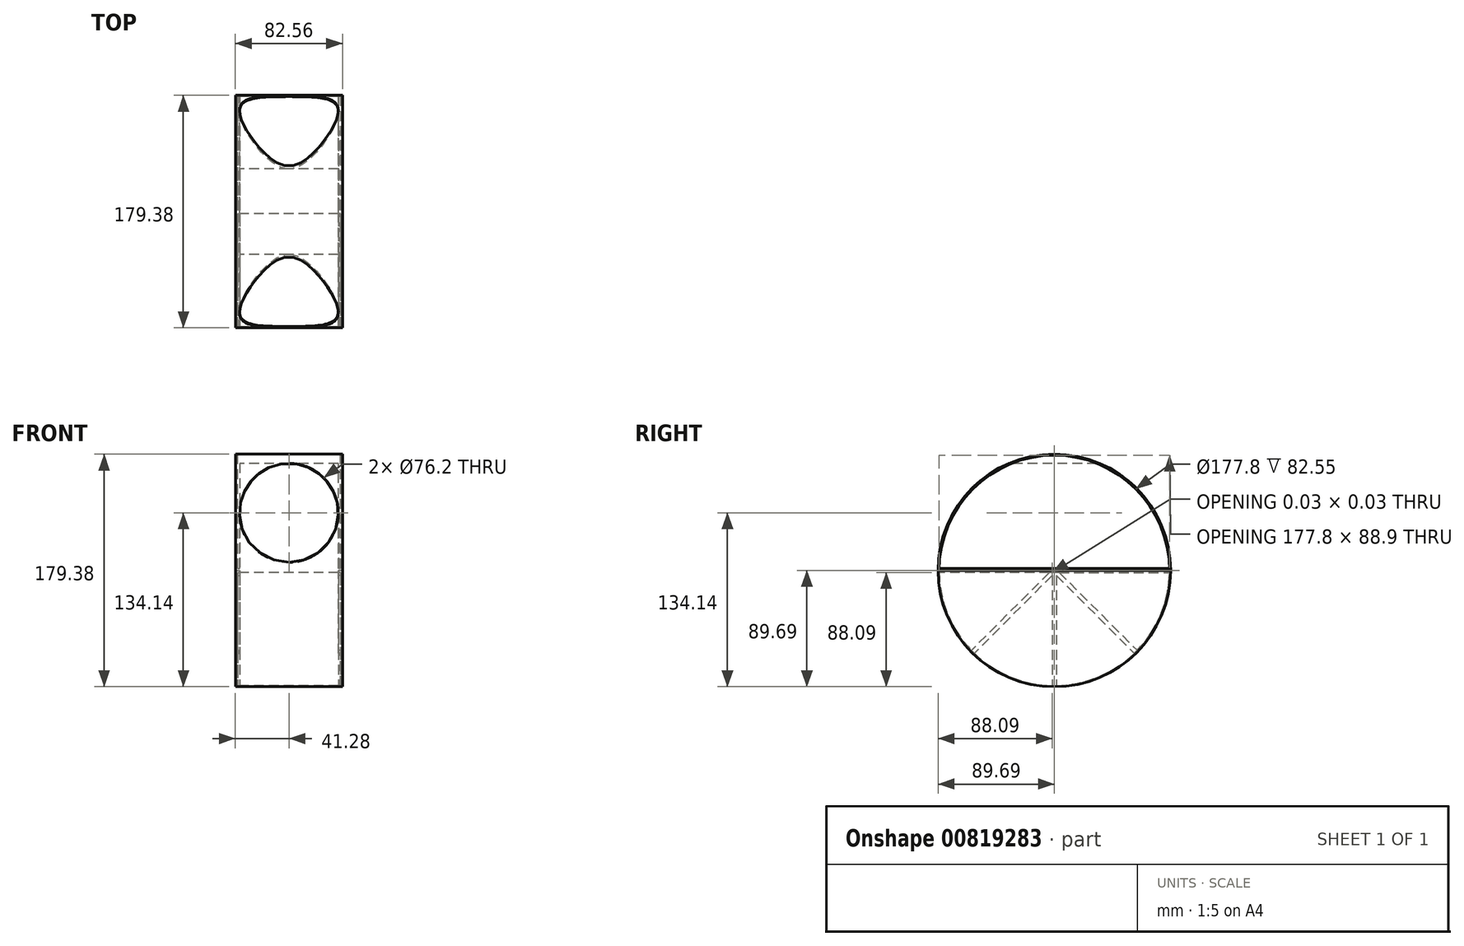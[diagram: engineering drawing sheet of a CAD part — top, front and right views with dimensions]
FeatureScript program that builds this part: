
annotation { "Feature Type Name" : "Feature", "Feature Type Description" : "" }
export const myFeature = defineFeature(function(context is Context, id is Id, definition is map)
    precondition{}
    {
        {
            var Q0;
            Q0=qCreatedBy(makeId("Right.planeOp"),FACE);
            var sketch = newSketch(context, id + "F0", { "sketchPlane" : qUnion([Q0])});
            skCircle(sketch, "E0", {"center": v(0, 0) * mm, "radius": 88.9 * mm});
            skLineSegment(sketch, "E1", {"start": v(0, 0) * mm, "end": v(88.9, 0) * mm});
            skLineSegment(sketch, "E2", {"start": v(88.9, 0) * mm, "end": v(0, 0) * mm});
            skLineSegment(sketch, "E3.4.0", {"start": v(0, 0) * mm, "end": v(-88.9, 0) * mm});
            skLineSegment(sketch, "E3.5.0", {"start": v(-1.59, -1.59) * mm, "end": v(-62.86, -62.86) * mm});
            skLineSegment(sketch, "E3.6.0", {"start": v(0, -1.59) * mm, "end": v(0, -88.9) * mm});
            skLineSegment(sketch, "E3.7.0", {"start": v(1.59, -1.59) * mm, "end": v(62.86, -62.86) * mm});
            skLineSegment(sketch, "E4", {"start": v(0, 6.35) * mm, "end": v(88.67, 6.35) * mm});
            skLineSegment(sketch, "E5", {"start": v(0, 82.55) * mm, "end": v(33, 82.55) * mm});
            skLineSegment(sketch, "E6", {"start": v(0, 6.35) * mm, "end": v(-88.67, 6.35) * mm});
            skLineSegment(sketch, "E7", {"start": v(0, 82.55) * mm, "end": v(-33, 82.55) * mm});
            skLineSegment(sketch, "E8.0", {"start": v(0, 1.59) * mm, "end": v(-88.89, 1.59) * mm});
            skLineSegment(sketch, "E9.0", {"start": v(-1.59, -1.61) * mm, "end": v(-1.61, -1.61) * mm});
            skLineSegment(sketch, "E10.0", {"start": v(0, 1.59) * mm, "end": v(88.89, 1.59) * mm});
            skLineSegment(sketch, "E11.1", {"start": v(3.83, -1.59) * mm, "end": v(63.97, -61.73) * mm});
            skLineSegment(sketch, "E12.0", {"start": v(-1.59, -3.83) * mm, "end": v(-61.73, -63.97) * mm});
            skLineSegment(sketch, "E12.1", {"start": v(1.59, -3.83) * mm, "end": v(61.73, -63.97) * mm});
            skLineSegment(sketch, "E13.0", {"start": v(-1.59, -1.59) * mm, "end": v(-1.59, -1.61) * mm});
            skLineSegment(sketch, "E14.trimOffspring", {"start": v(1.59, -3.83) * mm, "end": v(1.59, -88.89) * mm});
            skLineSegment(sketch, "E15.trimOffspring", {"start": v(-1.59, -3.83) * mm, "end": v(-1.59, -88.89) * mm});
            skLineSegment(sketch, "E16.trimOffspring", {"start": v(-3.86, -1.61) * mm, "end": v(-88.89, -1.61) * mm});
            skLineSegment(sketch, "E17.trimOffspring", {"start": v(-3.86, -1.61) * mm, "end": v(-63.97, -61.73) * mm});
            skLineSegment(sketch, "E18.trimOffspring", {"start": v(3.83, -1.59) * mm, "end": v(88.89, -1.59) * mm});
            skSolve(sketch);
        }
        {
            var Q0;
            {var subQ0=sQuery(id+"F0.wireOp",EDGE,"E2");Q0=makeQuery(id+"F0.imprint","IMPRINT",FACE,{"disambiguationData":[TD([[makeQuery(id+"F0.imprint","IMPRINT",EDGE,{"derivedFrom":subQ0}),1.0]])]});}
            var Q1;
            {var subQ0=sQuery(id+"F0.wireOp",EDGE,"E2");Q1=makeQuery(id+"F0.imprint","IMPRINT",FACE,{"disambiguationData":[TD([[makeQuery(id+"F0.imprint","IMPRINT",EDGE,{"derivedFrom":subQ0}),-1.0]])]});}
            var Q2;
            {var subQ1=sQuery(id+"F0.wireOp",EDGE,"E4");Q2=makeQuery(id+"F0.imprint","IMPRINT",FACE,{"disambiguationData":[TD([[makeQuery(id+"F0.imprint","IMPRINT",EDGE,{"derivedFrom":subQ1}),1.0]])]});}
            var Q3;
            {var subQ0=sQuery(id+"F0.wireOp",EDGE,"E3.4.0");Q3=makeQuery(id+"F0.imprint","IMPRINT",FACE,{"disambiguationData":[TD([[makeQuery(id+"F0.imprint","IMPRINT",EDGE,{"derivedFrom":subQ0}),1.0]])]});}
            var Q4;
            {var subQ0=sQuery(id+"F0.wireOp",EDGE,"E5");Q4=makeQuery(id+"F0.imprint","IMPRINT",FACE,{"disambiguationData":[TD([[makeQuery(id+"F0.imprint","IMPRINT",EDGE,{"derivedFrom":subQ0}),1.0]])]});}
            var Q5;
            {var subQ0=sQuery(id+"F0.wireOp",EDGE,"E3.5.0");Q5=makeQuery(id+"F0.imprint","IMPRINT",FACE,{"disambiguationData":[TD([[makeQuery(id+"F0.imprint","IMPRINT",EDGE,{"derivedFrom":subQ0}),1.0]])]});}
            var Q6;
            {var subQ1=sQuery(id+"F0.wireOp",EDGE,"E4");Q6=makeQuery(id+"F0.imprint","IMPRINT",FACE,{"disambiguationData":[TD([[makeQuery(id+"F0.imprint","IMPRINT",EDGE,{"derivedFrom":subQ1}),-1.0]])]});}
            extrude(context, id + "F1", {"entities" : qUnion([Q0, Q1, Q2, Q3, Q4, Q5, Q6]), "oppositeDirection" : true, "depth" : 39.69 * mm, "offsetDistance" : 25.4 * mm, "hasSecondDirection" : true, "secondDirectionOppositeDirection" : true, "secondDirectionDepth" : 38.1 * mm});
        }
        {
            var Q0;
            {var subQ0=sQuery(id+"F0.wireOp",EDGE,"E2");Q0=makeQuery(id+"F0.imprint","IMPRINT",FACE,{"disambiguationData":[TD([[makeQuery(id+"F0.imprint","IMPRINT",EDGE,{"derivedFrom":subQ0}),-1.0]])]});}
            var Q1;
            {var subQ0=sQuery(id+"F0.wireOp",EDGE,"E5");Q1=makeQuery(id+"F0.imprint","IMPRINT",FACE,{"disambiguationData":[TD([[makeQuery(id+"F0.imprint","IMPRINT",EDGE,{"derivedFrom":subQ0}),1.0]])]});}
            var Q2;
            {var subQ0=sQuery(id+"F0.wireOp",EDGE,"E3.4.0");Q2=makeQuery(id+"F0.imprint","IMPRINT",FACE,{"disambiguationData":[TD([[makeQuery(id+"F0.imprint","IMPRINT",EDGE,{"derivedFrom":subQ0}),1.0]])]});}
            var Q3;
            {var subQ0=sQuery(id+"F0.wireOp",EDGE,"E2");Q3=makeQuery(id+"F0.imprint","IMPRINT",FACE,{"disambiguationData":[TD([[makeQuery(id+"F0.imprint","IMPRINT",EDGE,{"derivedFrom":subQ0}),1.0]])]});}
            var Q4;
            {var subQ0=sQuery(id+"F0.wireOp",EDGE,"E3.5.0");Q4=makeQuery(id+"F0.imprint","IMPRINT",FACE,{"disambiguationData":[TD([[makeQuery(id+"F0.imprint","IMPRINT",EDGE,{"derivedFrom":subQ0}),1.0]])]});}
            var Q5;
            {var subQ1=sQuery(id+"F0.wireOp",EDGE,"E4");Q5=makeQuery(id+"F0.imprint","IMPRINT",FACE,{"disambiguationData":[TD([[makeQuery(id+"F0.imprint","IMPRINT",EDGE,{"derivedFrom":subQ1}),1.0]])]});}
            var Q6;
            {var subQ1=sQuery(id+"F0.wireOp",EDGE,"E4");Q6=makeQuery(id+"F0.imprint","IMPRINT",FACE,{"disambiguationData":[TD([[makeQuery(id+"F0.imprint","IMPRINT",EDGE,{"derivedFrom":subQ1}),-1.0]])]});}
            var Q7;
            {var subQ0=sQuery(id+"F0.wireOp",EDGE,"E11.1");Q7=makeQuery(id+"F0.imprint","IMPRINT",FACE,{"disambiguationData":[TD([[makeQuery(id+"F0.imprint","IMPRINT",EDGE,{"derivedFrom":subQ0}),1.0]])]});}
            extrude(context, id + "F2", {"entities" : qUnion([Q0, Q1, Q2, Q3, Q4, Q5, Q6, Q7]), "depth" : 39.69 * mm, "offsetDistance" : 25.4 * mm, "hasSecondDirection" : true, "secondDirectionOppositeDirection" : false, "secondDirectionDepth" : 38.1 * mm});
        }
        {
            var Q0;
            {var subQ0=sQuery(id+"F0.wireOp",EDGE,"E2");Q0=makeQuery(id+"F0.imprint","IMPRINT",FACE,{"disambiguationData":[TD([[makeQuery(id+"F0.imprint","IMPRINT",EDGE,{"derivedFrom":subQ0}),-1.0]])]});}
            var Q1;
            {var subQ0=sQuery(id+"F0.wireOp",EDGE,"E5");Q1=makeQuery(id+"F0.imprint","IMPRINT",FACE,{"disambiguationData":[TD([[makeQuery(id+"F0.imprint","IMPRINT",EDGE,{"derivedFrom":subQ0}),1.0]])]});}
            var Q2;
            {var subQ0=sQuery(id+"F0.wireOp",EDGE,"E2");Q2=makeQuery(id+"F0.imprint","IMPRINT",FACE,{"disambiguationData":[TD([[makeQuery(id+"F0.imprint","IMPRINT",EDGE,{"derivedFrom":subQ0}),1.0]])]});}
            var Q3;
            {var subQ0=sQuery(id+"F0.wireOp",EDGE,"E3.6.0");Q3=makeQuery(id+"F0.imprint","IMPRINT",FACE,{"disambiguationData":[TD([[makeQuery(id+"F0.imprint","IMPRINT",EDGE,{"derivedFrom":subQ0}),1.0]])]});}
            var Q4;
            {var subQ0=sQuery(id+"F0.wireOp",EDGE,"E3.5.0");Q4=makeQuery(id+"F0.imprint","IMPRINT",FACE,{"disambiguationData":[TD([[makeQuery(id+"F0.imprint","IMPRINT",EDGE,{"derivedFrom":subQ0}),1.0]])]});}
            extrude(context, id + "F3", {"entities" : qUnion([Q0, Q1, Q2, Q3, Q4]), "operationType" : NewBodyOperationType.ADD, "endBound" : BoundingType.SYMMETRIC, "depth" : 76.2 * mm, "offsetDistance" : 25.4 * mm});
        }
        {
            var Q0;
            Q0=qCreatedBy(makeId("Right.planeOp"),FACE);
            var sketch = newSketch(context, id + "F4", { "sketchPlane" : qUnion([Q0])});
            skCircle(sketch, "E19", {"center": v(0, 0) * mm, "radius": 88.9 * mm});
            skCircle(sketch, "E20", {"center": v(0, 0) * mm, "radius": 89.7 * mm});
            skLineSegment(sketch, "E21", {"start": v(0, 0) * mm, "end": v(88.9, 0) * mm});
            skLineSegment(sketch, "E22", {"start": v(0, 0) * mm, "end": v(-88.9, 0) * mm});
            skSolve(sketch);
        }
        {
            var Q0;
            Q0=makeQuery(id+"F4.imprint","IMPRINT",FACE,{"disambiguationData":[TD([[makeQuery(id+"F4.imprint","IMPRINT",EDGE,{"derivedFrom":sQuery(id+"F4.wireOp",EDGE,"E20")}),1.0]])]});
            extrude(context, id + "F5", {"entities" : qUnion([Q0]), "depth" : 39.69 * mm, "offsetDistance" : 25.4 * mm, "hasSecondDirection" : true, "secondDirectionOppositeDirection" : true, "secondDirectionDepth" : 39.69 * mm});
        }
        {
            var Q0;
            Q0=qCreatedBy(makeId("Front.planeOp"),FACE);
            var sketch = newSketch(context, id + "F6", { "sketchPlane" : qUnion([Q0])});
            skLineSegment(sketch, "E23", {"start": v(0, 0) * mm, "end": v(0, 44.45) * mm});
            skCircle(sketch, "E24", {"center": v(0, 44.45) * mm, "radius": 38.1 * mm});
            skSolve(sketch);
        }
        {
            var Q0;
            Q0=makeQuery(id+"F6.imprint","IMPRINT",FACE,{"disambiguationData":[TD([[makeQuery(id+"F6.imprint","IMPRINT",EDGE,{"derivedFrom":sQuery(id+"F6.wireOp",EDGE,"E24")}),1.0]])]});
            extrude(context, id + "F7", {"entities" : qUnion([Q0]), "operationType" : NewBodyOperationType.REMOVE, "endBound" : BoundingType.SYMMETRIC, "oppositeDirection" : true, "depth" : 190.5 * mm, "offsetDistance" : 25.4 * mm});
        }
        {
            var Q0;
            {var subQ0=sQuery(id+"F4.wireOp",EDGE,"E21");Q0=makeQuery(id+"F4.imprint","IMPRINT",FACE,{"disambiguationData":[TD([[makeQuery(id+"F4.imprint","IMPRINT",EDGE,{"derivedFrom":subQ0}),-1.0]])]});}
            var Q1;
            Q1=makeQuery(id+"F4.imprint","IMPRINT",FACE,{"disambiguationData":[TD([[makeQuery(id+"F4.imprint","IMPRINT",EDGE,{"derivedFrom":sQuery(id+"F4.wireOp",EDGE,"E20")}),1.0]])]});
            extrude(context, id + "F8", {"entities" : qUnion([Q0, Q1]), "operationType" : NewBodyOperationType.ADD, "depth" : 41.27 * mm, "offsetDistance" : 25.4 * mm, "hasSecondDirection" : true, "secondDirectionOppositeDirection" : false, "secondDirectionDepth" : 39.69 * mm});
        }
        {
            var Q0;
            Q0=makeQuery(id+"F4.imprint","IMPRINT",FACE,{"disambiguationData":[TD([[makeQuery(id+"F4.imprint","IMPRINT",EDGE,{"derivedFrom":sQuery(id+"F4.wireOp",EDGE,"E20")}),1.0]])]});
            var Q1;
            {var subQ0=sQuery(id+"F4.wireOp",EDGE,"E21");Q1=makeQuery(id+"F4.imprint","IMPRINT",FACE,{"disambiguationData":[TD([[makeQuery(id+"F4.imprint","IMPRINT",EDGE,{"derivedFrom":subQ0}),-1.0]])]});}
            extrude(context, id + "F9", {"entities" : qUnion([Q0, Q1]), "operationType" : NewBodyOperationType.ADD, "oppositeDirection" : true, "depth" : 41.27 * mm, "offsetDistance" : 25.4 * mm, "hasSecondDirection" : true, "secondDirectionOppositeDirection" : true, "secondDirectionDepth" : 39.69 * mm});
        }
    });
